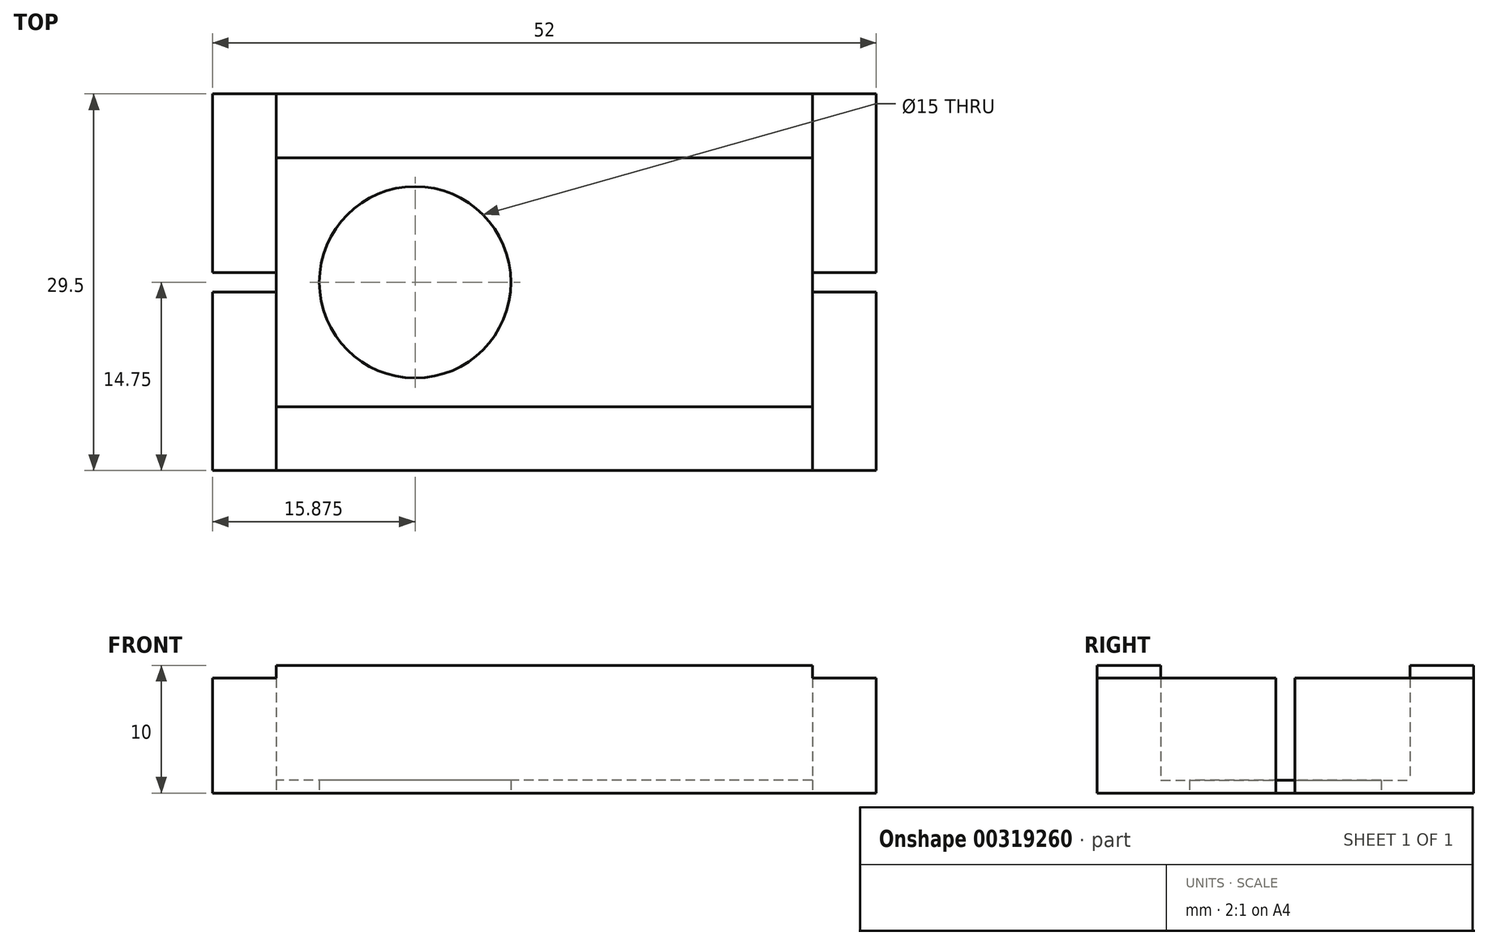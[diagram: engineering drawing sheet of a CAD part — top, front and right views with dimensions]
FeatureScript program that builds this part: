
annotation { "Feature Type Name" : "Feature", "Feature Type Description" : "" }
export const myFeature = defineFeature(function(context is Context, id is Id, definition is map)
    precondition{}
    {
        {
            var Q0;
            Q0=qCreatedBy(makeId("Top.planeOp"),FACE);
            var sketch = newSketch(context, id + "F0", { "sketchPlane" : qUnion([Q0])});
            skLineSegment(sketch, "E0.bottom", {"start": v(21, -9.75) * mm, "end": v(-21, -9.75) * mm});
            skLineSegment(sketch, "E0.top", {"start": v(21, 9.75) * mm, "end": v(-21, 9.75) * mm});
            skLineSegment(sketch, "E0.left", {"start": v(21, -9.75) * mm, "end": v(21, 9.75) * mm});
            skLineSegment(sketch, "E0.right", {"start": v(-21, -9.75) * mm, "end": v(-21, 9.75) * mm});
            skPoint(sketch, "E0.middle", {"position": v(0, 0) * mm});
            skLineSegment(sketch, "E1", {"start": v(0, 0) * mm, "end": v(0.75, 0) * mm});
            skLineSegment(sketch, "E2", {"start": v(0.75, 0) * mm, "end": v(0.75, -8.25) * mm});
            skLineSegment(sketch, "E3.MirrorCS", {"start": v(0.75, 0) * mm, "end": v(0.75, 8.25) * mm});
            skLineSegment(sketch, "E4", {"start": v(0.75, 8.25) * mm, "end": v(-18.5, 8.25) * mm});
            skLineSegment(sketch, "E5.MirrorCS", {"start": v(0.75, -8.25) * mm, "end": v(-18.5, -8.25) * mm});
            skLineSegment(sketch, "E6", {"start": v(-18.5, 8.25) * mm, "end": v(-18.5, -8.25) * mm});
            skLineSegment(sketch, "E7", {"start": v(0, 0) * mm, "end": v(-8.88, 0) * mm});
            skLineSegment(sketch, "E8", {"start": v(-8.88, 0) * mm, "end": v(-10.12, 0) * mm});
            skCircle(sketch, "E9", {"center": v(-10.12, 0) * mm, "radius": 1.25 * mm});
            skCircle(sketch, "E10", {"center": v(-10.12, 0) * mm, "radius": 2.5 * mm});
            skCircle(sketch, "E11", {"center": v(-10.12, 0) * mm, "radius": 3 * mm});
            skCircle(sketch, "E12", {"center": v(-10.12, 0) * mm, "radius": 7.5 * mm});
            skSolve(sketch);
        }
        {
            var Q0;
            Q0=makeQuery(id+"F0.imprint","IMPRINT",FACE,{"disambiguationData":[TD([[makeQuery(id+"F0.imprint","IMPRINT",EDGE,{"derivedFrom":sQuery(id+"F0.wireOp",EDGE,"E0.bottom")}),-1.0]])]});
            var Q1;
            Q1=makeQuery(id+"F0.imprint","IMPRINT",FACE,{"disambiguationData":[TD([[makeQuery(id+"F0.imprint","IMPRINT",EDGE,{"derivedFrom":sQuery(id+"F0.wireOp",EDGE,"E2")}),-1.0]])]});
            extrude(context, id + "F1", {"entities" : qUnion([Q0, Q1]), "depth" : 1 * mm});
        }
        {
            var Q0;
            Q0=qCreatedBy(makeId("Top.planeOp"),FACE);
            var sketch = newSketch(context, id + "F2", { "sketchPlane" : qUnion([Q0])});
            skLineSegment(sketch, "E13.bottom", {"start": v(-21, 14.75) * mm, "end": v(21, 14.75) * mm});
            skLineSegment(sketch, "E13.top", {"start": v(-21, 9.75) * mm, "end": v(21, 9.75) * mm});
            skLineSegment(sketch, "E13.left", {"start": v(-21, 14.75) * mm, "end": v(-21, 9.75) * mm});
            skLineSegment(sketch, "E13.right", {"start": v(21, 14.75) * mm, "end": v(21, 9.75) * mm});
            skLineSegment(sketch, "E14.MirrorCS", {"start": v(-21, -14.75) * mm, "end": v(-21, -9.75) * mm});
            skLineSegment(sketch, "E15.MirrorCS", {"start": v(-21, -14.75) * mm, "end": v(21, -14.75) * mm});
            skLineSegment(sketch, "E16.MirrorCS", {"start": v(21, -14.75) * mm, "end": v(21, -9.75) * mm});
            skLineSegment(sketch, "E17.bottom", {"start": v(-21, 14.75) * mm, "end": v(-26, 14.75) * mm});
            skLineSegment(sketch, "E17.top", {"start": v(-21, -14.75) * mm, "end": v(-26, -14.75) * mm});
            skLineSegment(sketch, "E17.left", {"start": v(-21, 14.75) * mm, "end": v(-21, -14.75) * mm});
            skLineSegment(sketch, "E17.right", {"start": v(-26, 14.75) * mm, "end": v(-26, -14.75) * mm});
            skLineSegment(sketch, "E18.MirrorCS", {"start": v(26, 14.75) * mm, "end": v(26, -14.75) * mm});
            skLineSegment(sketch, "E19.MirrorCS", {"start": v(21, 14.75) * mm, "end": v(26, 14.75) * mm});
            skLineSegment(sketch, "E20.MirrorCS", {"start": v(21, -14.75) * mm, "end": v(26, -14.75) * mm});
            skLineSegment(sketch, "E21.left", {"start": v(-26, 0) * mm, "end": v(-26, 0.75) * mm});
            skLineSegment(sketch, "E21.right", {"start": v(-21, 0) * mm, "end": v(-21, 0.75) * mm});
            skLineSegment(sketch, "E22.bottom", {"start": v(26, 0) * mm, "end": v(21, 0) * mm});
            skLineSegment(sketch, "E23", {"start": v(21, 0) * mm, "end": v(26, 0) * mm});
            skLineSegment(sketch, "E24.top", {"start": v(21, 0.75) * mm, "end": v(26, 0.75) * mm});
            skLineSegment(sketch, "E24.left", {"start": v(21, 0) * mm, "end": v(21, 0.75) * mm});
            skLineSegment(sketch, "E24.right", {"start": v(26, 0) * mm, "end": v(26, 0.75) * mm});
            skLineSegment(sketch, "E25.MirrorCS", {"start": v(21, -0.75) * mm, "end": v(26, -0.75) * mm});
            skLineSegment(sketch, "E26.MirrorCS", {"start": v(26, 0) * mm, "end": v(26, -0.75) * mm});
            skLineSegment(sketch, "E27.MirrorCS", {"start": v(21, 0) * mm, "end": v(21, -0.75) * mm});
            skLineSegment(sketch, "E28", {"start": v(21, 0.75) * mm, "end": v(21, 14.75) * mm});
            skLineSegment(sketch, "E29", {"start": v(26, 14.75) * mm, "end": v(26, 0.75) * mm});
            skLineSegment(sketch, "E30", {"start": v(26, -0.75) * mm, "end": v(26, -14.75) * mm});
            skLineSegment(sketch, "E31", {"start": v(21, -14.75) * mm, "end": v(21, -0.75) * mm});
            skLineSegment(sketch, "E32", {"start": v(-21, -9.75) * mm, "end": v(21, -9.75) * mm});
            skLineSegment(sketch, "E33", {"start": v(21, 9.75) * mm, "end": v(21, -9.75) * mm});
            skLineSegment(sketch, "E34", {"start": v(-21, 9.75) * mm, "end": v(-21, -9.75) * mm});
            skLineSegment(sketch, "E35", {"start": v(21, -9.75) * mm, "end": v(21, 9.75) * mm});
            skLineSegment(sketch, "E36.MirrorCS", {"start": v(-21, 0.75) * mm, "end": v(-26, 0.75) * mm});
            skLineSegment(sketch, "E37.MirrorCS", {"start": v(-21, -0.75) * mm, "end": v(-26, -0.75) * mm});
            skLineSegment(sketch, "E38.MirrorCS", {"start": v(-21, 0) * mm, "end": v(-26, 0) * mm});
            skSolve(sketch);
        }
        {
            var Q0;
            {var subQ0=sQuery(id+"F2.wireOp",EDGE,"E13.bottom");Q0=makeQuery(id+"F2.imprint","IMPRINT",FACE,{"disambiguationData":[TD([[makeQuery(id+"F2.imprint","IMPRINT",EDGE,{"derivedFrom":subQ0}),-1.0]])]});}
            var Q1;
            {var subQ0=sQuery(id+"F2.wireOp",EDGE,"E15.MirrorCS");Q1=makeQuery(id+"F2.imprint","IMPRINT",FACE,{"disambiguationData":[TD([[makeQuery(id+"F2.imprint","IMPRINT",EDGE,{"derivedFrom":subQ0}),1.0]])]});}
            extrude(context, id + "F3", {"entities" : qUnion([Q0, Q1]), "operationType" : NewBodyOperationType.ADD, "depth" : 10 * mm});
        }
        {
            var Q0;
            {var subQ1=sQuery(id+"F2.wireOp",EDGE,"E17.top");Q0=makeQuery(id+"F2.imprint","IMPRINT",FACE,{"disambiguationData":[TD([[makeQuery(id+"F2.imprint","IMPRINT",EDGE,{"derivedFrom":subQ1}),-1.0]])]});}
            var Q1;
            Q1=makeQuery(id+"F2.imprint","IMPRINT",FACE,{"disambiguationData":[TD([[makeQuery(id+"F2.imprint","IMPRINT",EDGE,{"derivedFrom":sQuery(id+"F2.wireOp",EDGE,"E19.MirrorCS")}),-1.0]])]});
            var Q2;
            Q2=makeQuery(id+"F2.imprint","IMPRINT",FACE,{"disambiguationData":[TD([[makeQuery(id+"F2.imprint","IMPRINT",EDGE,{"derivedFrom":sQuery(id+"F2.wireOp",EDGE,"E20.MirrorCS")}),1.0]])]});
            var Q3;
            {var subQ2=sQuery(id+"F2.wireOp",EDGE,"E17.bottom");Q3=makeQuery(id+"F2.imprint","IMPRINT",FACE,{"disambiguationData":[TD([[makeQuery(id+"F2.imprint","IMPRINT",EDGE,{"derivedFrom":subQ2}),1.0]])]});}
            extrude(context, id + "F4", {"entities" : qUnion([Q0, Q1, Q2, Q3]), "operationType" : NewBodyOperationType.ADD, "depth" : 9 * mm});
        }
    });
